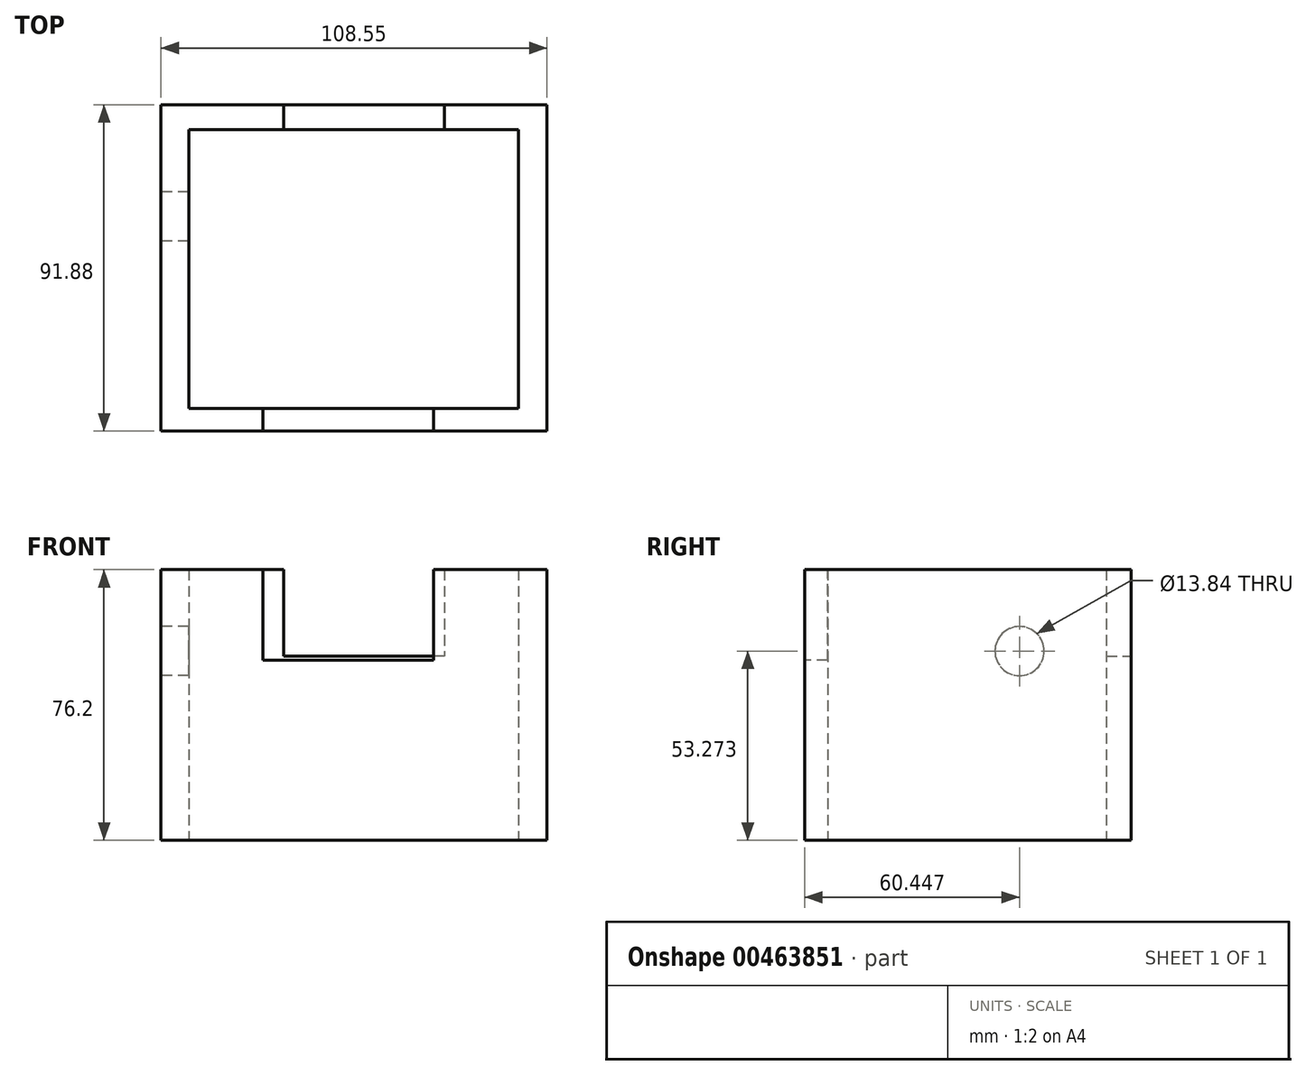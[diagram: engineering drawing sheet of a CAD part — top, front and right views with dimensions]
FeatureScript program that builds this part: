
annotation { "Feature Type Name" : "Feature", "Feature Type Description" : "" }
export const myFeature = defineFeature(function(context is Context, id is Id, definition is map)
    precondition{}
    {
        {
            var Q0;
            Q0=qCreatedBy(makeId("Top.planeOp"),FACE);
            var sketch = newSketch(context, id + "F0", { "sketchPlane" : qUnion([Q0])});
            skLineSegment(sketch, "E0.bottom", {"start": v(-47.35, -43.31) * mm, "end": v(61.2, -43.31) * mm});
            skLineSegment(sketch, "E0.top", {"start": v(-47.35, 48.57) * mm, "end": v(61.2, 48.57) * mm});
            skLineSegment(sketch, "E0.left", {"start": v(-47.35, -43.31) * mm, "end": v(-47.35, 48.57) * mm});
            skLineSegment(sketch, "E0.right", {"start": v(61.2, -43.31) * mm, "end": v(61.2, 48.57) * mm});
            skSolve(sketch);
        }
        {
            var Q0;
            Q0=makeQuery(id+"F0.imprint","IMPRINT",FACE,{"disambiguationData":[TD([[makeQuery(id+"F0.imprint","IMPRINT",EDGE,{"derivedFrom":sQuery(id+"F0.wireOp",EDGE,"E0.bottom")}),1.0]])]});
            extrude(context, id + "F1", {"entities" : qUnion([Q0]), "depth" : 76.2 * mm});
        }
        {
            var Q0;
            Q0=qCreatedBy(makeId("Top.planeOp"),FACE);
            var sketch = newSketch(context, id + "F2", { "sketchPlane" : qUnion([Q0])});
            skLineSegment(sketch, "E1.bottom", {"start": v(-39.6, -36.86) * mm, "end": v(53.24, -36.86) * mm});
            skLineSegment(sketch, "E1.top", {"start": v(-39.6, 41.56) * mm, "end": v(53.24, 41.56) * mm});
            skLineSegment(sketch, "E1.left", {"start": v(-39.6, -36.86) * mm, "end": v(-39.6, 41.56) * mm});
            skLineSegment(sketch, "E1.right", {"start": v(53.24, -36.86) * mm, "end": v(53.24, 41.56) * mm});
            skSolve(sketch);
        }
        {
            var Q0;
            Q0=makeQuery(id+"F2.imprint","IMPRINT",FACE,{"disambiguationData":[TD([[makeQuery(id+"F2.imprint","IMPRINT",EDGE,{"derivedFrom":sQuery(id+"F2.wireOp",EDGE,"E1.bottom")}),1.0]])]});
            extrude(context, id + "F3", {"entities" : qUnion([Q0]), "operationType" : NewBodyOperationType.REMOVE, "depth" : 82.55 * mm});
        }
        {
            var Q0;
            Q0=makeQuery(id+"F1.opExtrude","SWEPT_FACE",FACE,{"disambiguationData":[OSD([sQuery(id+"F0.wireOp",EDGE,"E0.left")])]});
            var sketch = newSketch(context, id + "F4", { "sketchPlane" : qUnion([Q0])});
            skSolve(sketch);
        }
        {
            var Q0;
            {var subQ0=sQuery(id+"F0.wireOp",EDGE,"E0.left");Q0=makeQuery(id+"F4.imprint","IMPRINT",FACE,{"disambiguationData":[TD([[makeQuery(id+"F4.imprint","IMPRINT",EDGE,{"derivedFrom":makeQuery(id+"F1.opExtrude","CAP_EDGE",EDGE,{"disambiguationData":[OSD([subQ0])],"isStart":true})}),-1.0]])]});}
            var sketch = newSketch(context, id + "F5", { "sketchPlane" : qUnion([Q0])});
            skCircle(sketch, "E2", {"center": v(-17.14, 53.27) * mm, "radius": 6.92 * mm});
            skSolve(sketch);
        }
        {
            var Q0;
            Q0=makeQuery(id+"F5.imprint","IMPRINT",FACE,{"disambiguationData":[TD([[makeQuery(id+"F5.imprint","IMPRINT",EDGE,{"derivedFrom":sQuery(id+"F5.wireOp",EDGE,"E2")}),1.0]])]});
            extrude(context, id + "F6", {"entities" : qUnion([Q0]), "operationType" : NewBodyOperationType.REMOVE, "oppositeDirection" : true, "depth" : 25.4 * mm});
        }
        {
            var Q0;
            Q0=makeQuery(id+"F1.opExtrude","SWEPT_FACE",FACE,{"disambiguationData":[OSD([sQuery(id+"F0.wireOp",EDGE,"E0.bottom")])]});
            var sketch = newSketch(context, id + "F7", { "sketchPlane" : qUnion([Q0])});
            skLineSegment(sketch, "E3.bottom", {"start": v(-18.7, 76.2) * mm, "end": v(29.33, 76.2) * mm});
            skLineSegment(sketch, "E3.top", {"start": v(-18.7, 50.75) * mm, "end": v(29.33, 50.75) * mm});
            skLineSegment(sketch, "E3.left", {"start": v(-18.7, 76.2) * mm, "end": v(-18.7, 50.75) * mm});
            skLineSegment(sketch, "E3.right", {"start": v(29.33, 76.2) * mm, "end": v(29.33, 50.75) * mm});
            skSolve(sketch);
        }
        {
            var Q0;
            Q0=makeQuery(id+"F7.imprint","IMPRINT",FACE,{"disambiguationData":[TD([[makeQuery(id+"F7.imprint","IMPRINT",EDGE,{"derivedFrom":sQuery(id+"F7.wireOp",EDGE,"E3.bottom")}),-1.0]])]});
            extrude(context, id + "F8", {"entities" : qUnion([Q0]), "operationType" : NewBodyOperationType.REMOVE, "oppositeDirection" : true, "depth" : 25.4 * mm});
        }
        {
            var Q0;
            Q0=makeQuery(id+"F1.opExtrude","SWEPT_FACE",FACE,{"disambiguationData":[OSD([sQuery(id+"F0.wireOp",EDGE,"E0.top")])]});
            var sketch = newSketch(context, id + "F9", { "sketchPlane" : qUnion([Q0])});
            skLineSegment(sketch, "E4.bottom", {"start": v(-32.36, 76.2) * mm, "end": v(12.86, 76.2) * mm});
            skLineSegment(sketch, "E4.top", {"start": v(-32.36, 51.92) * mm, "end": v(12.86, 51.92) * mm});
            skLineSegment(sketch, "E4.left", {"start": v(-32.36, 76.2) * mm, "end": v(-32.36, 51.92) * mm});
            skLineSegment(sketch, "E4.right", {"start": v(12.86, 76.2) * mm, "end": v(12.86, 51.92) * mm});
            skSolve(sketch);
        }
        {
            var Q0;
            Q0=makeQuery(id+"F9.imprint","IMPRINT",FACE,{"disambiguationData":[TD([[makeQuery(id+"F9.imprint","IMPRINT",EDGE,{"derivedFrom":sQuery(id+"F9.wireOp",EDGE,"E4.bottom")}),1.0]])]});
            extrude(context, id + "F10", {"entities" : qUnion([Q0]), "operationType" : NewBodyOperationType.REMOVE, "oppositeDirection" : true, "depth" : 25.4 * mm});
        }
    });
